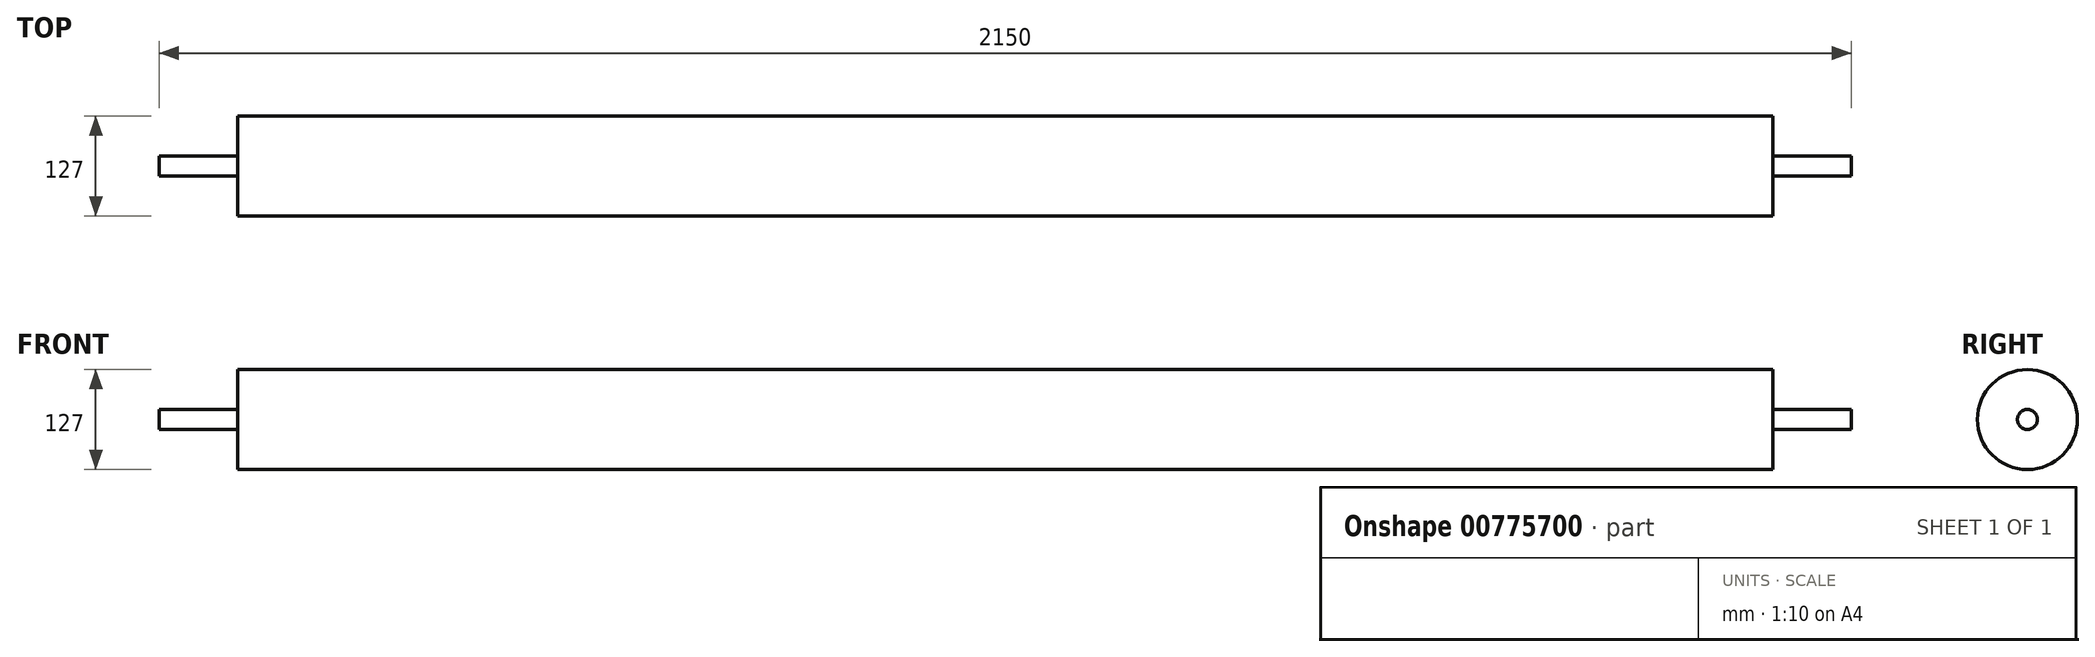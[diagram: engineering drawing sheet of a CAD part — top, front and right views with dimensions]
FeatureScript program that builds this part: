
annotation { "Feature Type Name" : "Feature", "Feature Type Description" : "" }
export const myFeature = defineFeature(function(context is Context, id is Id, definition is map)
    precondition{}
    {
        {
            var Q0;
            Q0=qCreatedBy(makeId("Front.planeOp"),FACE);
            var sketch = newSketch(context, id + "F0", { "sketchPlane" : qUnion([Q0])});
            skLineSegment(sketch, "E0", {"start": v(-1075, 0) * mm, "end": v(1075, 0) * mm});
            skLineSegment(sketch, "E1", {"start": v(1075, 0) * mm, "end": v(1075, 12.7) * mm});
            skLineSegment(sketch, "E2", {"start": v(1075, 12.7) * mm, "end": v(975, 12.7) * mm});
            skLineSegment(sketch, "E3", {"start": v(975, 12.7) * mm, "end": v(975, 63.5) * mm});
            skLineSegment(sketch, "E4", {"start": v(975, 63.5) * mm, "end": v(-975, 63.5) * mm});
            skLineSegment(sketch, "E5", {"start": v(-975, 63.5) * mm, "end": v(-975, 12.7) * mm});
            skLineSegment(sketch, "E6", {"start": v(-975, 12.7) * mm, "end": v(-1075, 12.7) * mm});
            skLineSegment(sketch, "E7", {"start": v(-1075, 12.7) * mm, "end": v(-1075, 0) * mm});
            skSolve(sketch);
        }
        {
            var Q0;
            Q0=makeQuery(id+"F0.imprint","IMPRINT",FACE,{"disambiguationData":[TD([[makeQuery(id+"F0.imprint","IMPRINT",EDGE,{"derivedFrom":sQuery(id+"F0.wireOp",EDGE,"E0")}),1.0]])]});
            var Q1;
            Q1=sQuery(id+"F0.wireOp",EDGE,"E0");
            revolve(context, id + "F1", {"surfaceOperationType" : NewSurfaceOperationType.NEW, "entities" : qUnion([Q0]), "axis" : qUnion([Q1]), "revolveType" : RevolveType.FULL});
        }
    });
